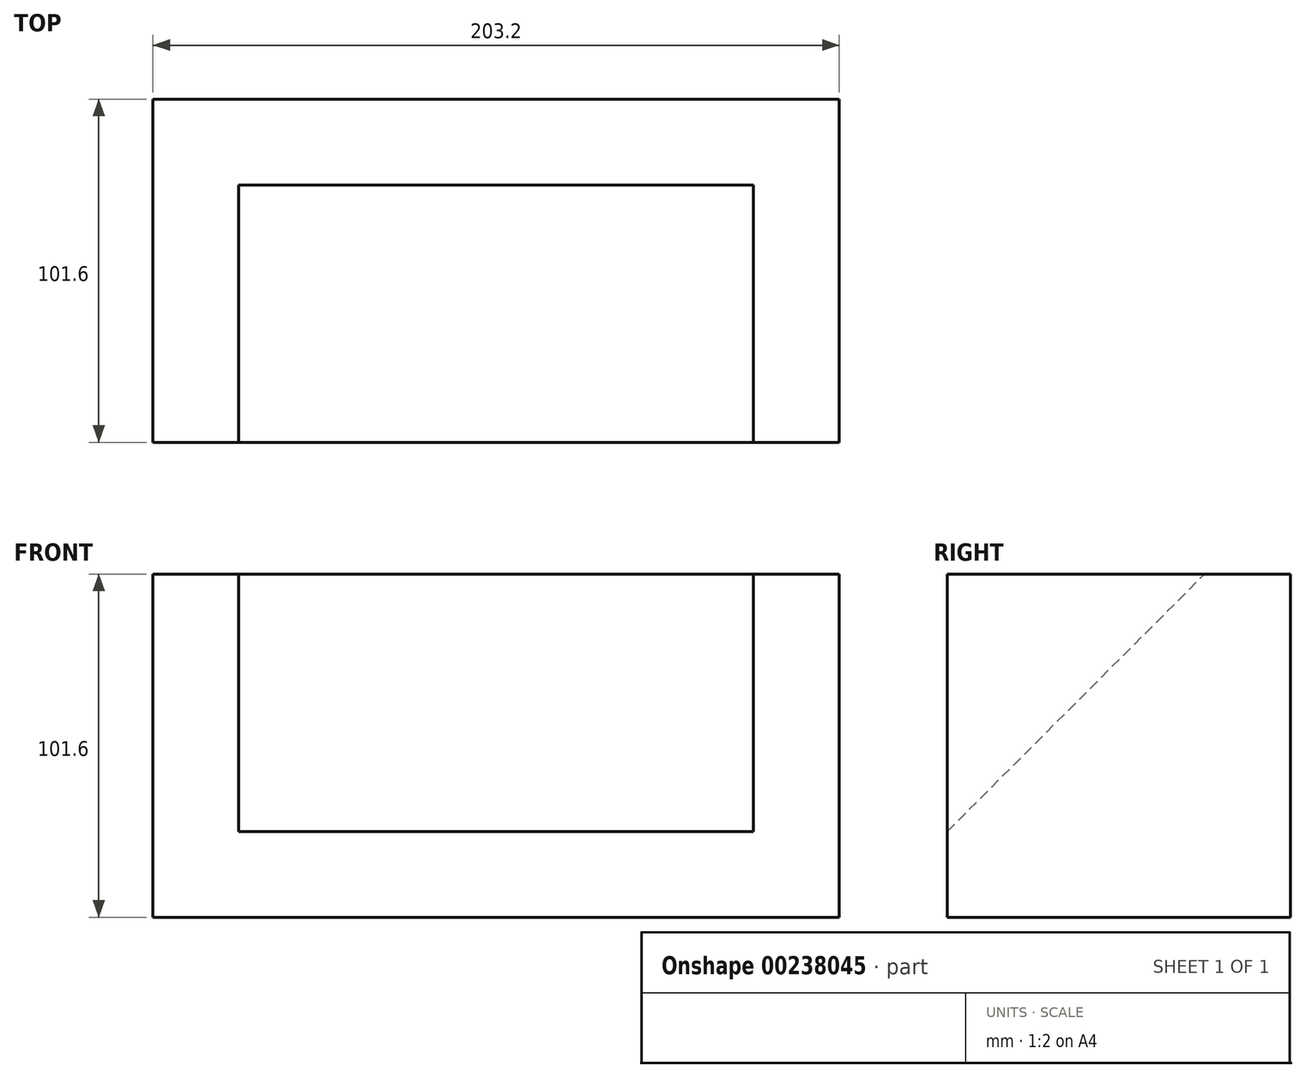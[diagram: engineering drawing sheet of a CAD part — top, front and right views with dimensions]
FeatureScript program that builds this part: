
annotation { "Feature Type Name" : "Feature", "Feature Type Description" : "" }
export const myFeature = defineFeature(function(context is Context, id is Id, definition is map)
    precondition{}
    {
        {
            var Q0;
            Q0=qCreatedBy(makeId("Front.planeOp"),FACE);
            var sketch = newSketch(context, id + "F0", { "sketchPlane" : qUnion([Q0])});
            skLineSegment(sketch, "E0.bottom", {"start": v(-125.75, 73.4) * mm, "end": v(77.45, 73.4) * mm});
            skLineSegment(sketch, "E0.top", {"start": v(-125.75, -28.2) * mm, "end": v(77.45, -28.2) * mm});
            skLineSegment(sketch, "E0.left", {"start": v(-125.75, 73.4) * mm, "end": v(-125.75, -28.2) * mm});
            skLineSegment(sketch, "E0.right", {"start": v(77.45, 73.4) * mm, "end": v(77.45, -28.2) * mm});
            skSolve(sketch);
        }
        {
            var Q0;
            Q0=makeQuery(id+"F0.imprint","IMPRINT",FACE,{"disambiguationData":[TD([[makeQuery(id+"F0.imprint","IMPRINT",EDGE,{"derivedFrom":sQuery(id+"F0.wireOp",EDGE,"E0.bottom")}),-1.0]])]});
            extrude(context, id + "F1", {"entities" : qUnion([Q0]), "depth" : 101.6 * mm});
        }
        {
            var Q0;
            Q0=makeQuery(id+"F1.opExtrude","CAP_FACE",FACE,{"disambiguationData":[OSD([sQuery(id+"F0.wireOp",EDGE,"E0.bottom"),sQuery(id+"F0.wireOp",EDGE,"E0.top"),sQuery(id+"F0.wireOp",EDGE,"E0.left"),sQuery(id+"F0.wireOp",EDGE,"E0.right")])],"isStart":false});
            var sketch = newSketch(context, id + "F2", { "sketchPlane" : qUnion([Q0])});
            skLineSegment(sketch, "E1.bottom", {"start": v(-100.35, 73.4) * mm, "end": v(52.05, 73.4) * mm});
            skLineSegment(sketch, "E1.top", {"start": v(-100.35, -2.8) * mm, "end": v(52.05, -2.8) * mm});
            skLineSegment(sketch, "E1.left", {"start": v(-100.35, 73.4) * mm, "end": v(-100.35, -2.8) * mm});
            skLineSegment(sketch, "E1.right", {"start": v(52.05, 73.4) * mm, "end": v(52.05, -2.8) * mm});
            skSolve(sketch);
        }
        {
            var Q0;
            Q0=makeQuery(id+"F2.imprint","IMPRINT",FACE,{"disambiguationData":[TD([[makeQuery(id+"F2.imprint","IMPRINT",EDGE,{"derivedFrom":sQuery(id+"F2.wireOp",EDGE,"E1.bottom")}),-1.0]])]});
            extrude(context, id + "F3", {"entities" : qUnion([Q0]), "operationType" : NewBodyOperationType.REMOVE, "oppositeDirection" : true, "depth" : 76.2 * mm});
        }
        {
            var Q0;
            Q0=makeQuery(id+"F3.boolean.opBoolean","COPY",FACE,{"derivedFrom":makeQuery(id+"F3.opExtrude","SWEPT_FACE",FACE,{"disambiguationData":[OSD([sQuery(id+"F2.wireOp",EDGE,"E1.left")])]})});
            var sketch = newSketch(context, id + "F4", { "sketchPlane" : qUnion([Q0])});
            skLineSegment(sketch, "E2", {"start": v(-101.6, -2.8) * mm, "end": v(-25.4, 73.4) * mm});
            skSolve(sketch);
        }
        {
            var Q0;
            Q0=makeQuery(id+"F4.imprint","IMPRINT",FACE,{"disambiguationData":[TD([[makeQuery(id+"F4.imprint","IMPRINT",EDGE,{"derivedFrom":sQuery(id+"F4.wireOp",EDGE,"E2")}),-1.0]])]});
            extrude(context, id + "F5", {"entities" : qUnion([Q0]), "operationType" : NewBodyOperationType.ADD, "depth" : 152.4 * mm});
        }
    });
